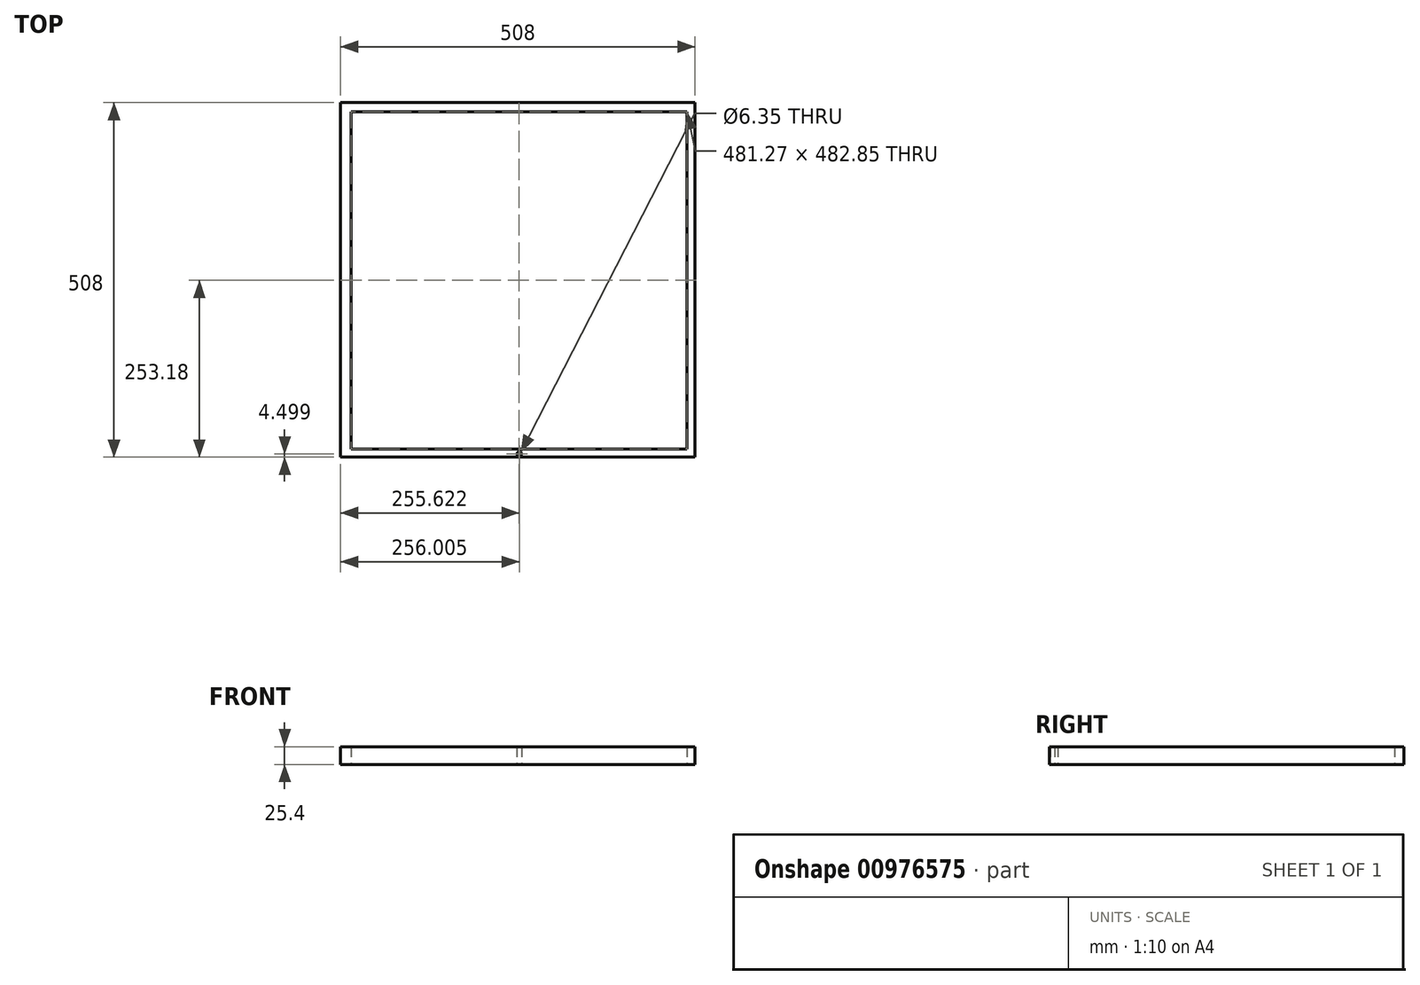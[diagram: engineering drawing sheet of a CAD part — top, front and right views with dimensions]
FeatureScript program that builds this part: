
annotation { "Feature Type Name" : "Feature", "Feature Type Description" : "" }
export const myFeature = defineFeature(function(context is Context, id is Id, definition is map)
    precondition{}
    {
        {
            var Q0;
            Q0=qCreatedBy(makeId("Top.planeOp"),FACE);
            var sketch = newSketch(context, id + "F0", { "sketchPlane" : qUnion([Q0])});
            skLineSegment(sketch, "E0.bottom", {"start": v(-306.53, 141.31) * mm, "end": v(-281.13, 141.31) * mm});
            skLineSegment(sketch, "E0.top", {"start": v(-306.53, -112.69) * mm, "end": v(-281.13, -112.69) * mm});
            skLineSegment(sketch, "E0.left", {"start": v(-306.53, 141.31) * mm, "end": v(-306.53, -112.69) * mm});
            skLineSegment(sketch, "E0.right", {"start": v(-281.13, 141.31) * mm, "end": v(-281.13, -112.69) * mm});
            skSolve(sketch);
        }
        {
            var Q0;
            Q0=makeQuery(id+"F0.imprint","IMPRINT",FACE,{"disambiguationData":[TD([[makeQuery(id+"F0.imprint","IMPRINT",EDGE,{"derivedFrom":sQuery(id+"F0.wireOp",EDGE,"E0.bottom")}),-1.0]])]});
            extrude(context, id + "F1", {"entities" : qUnion([Q0]), "depth" : 5.08 * mm, "offsetDistance" : 25.4 * mm});
        }
        {
            var Q0;
            Q0=makeQuery(id+"F1.opExtrude","SWEPT_BODY",BODY,{"disambiguationData":[OSD([sQuery(id+"F0.wireOp",EDGE,"E0.bottom"),sQuery(id+"F0.wireOp",EDGE,"E0.top"),sQuery(id+"F0.wireOp",EDGE,"E0.left"),sQuery(id+"F0.wireOp",EDGE,"E0.right")])]});
            deleteBodies(context, id + "F2", {"entities" : qUnion([Q0])});
        }
        {
            var Q0;
            Q0=qCreatedBy(makeId("Top.planeOp"),FACE);
            var sketch = newSketch(context, id + "F3", { "sketchPlane" : qUnion([Q0])});
            skLineSegment(sketch, "E1.bottom", {"start": v(-1811.36, 295.79) * mm, "end": v(-1303.36, 295.79) * mm});
            skLineSegment(sketch, "E1.top", {"start": v(-1811.36, -212.21) * mm, "end": v(-1303.36, -212.21) * mm});
            skLineSegment(sketch, "E1.left", {"start": v(-1811.36, 295.79) * mm, "end": v(-1811.36, -212.21) * mm});
            skLineSegment(sketch, "E1.right", {"start": v(-1303.36, 295.79) * mm, "end": v(-1303.36, -212.21) * mm});
            skSolve(sketch);
        }
        {
            var Q0;
            Q0=qCreatedBy(makeId("Top.planeOp"),FACE);
            var sketch = newSketch(context, id + "F4", { "sketchPlane" : qUnion([Q0])});
            skLineSegment(sketch, "E2.bottom", {"start": v(-482.6, 746.05) * mm, "end": v(0, 746.05) * mm});
            skLineSegment(sketch, "E2.top", {"start": v(-482.6, 263.45) * mm, "end": v(0, 263.45) * mm});
            skLineSegment(sketch, "E2.left", {"start": v(-482.6, 746.05) * mm, "end": v(-482.6, 263.45) * mm});
            skLineSegment(sketch, "E2.right", {"start": v(0, 746.05) * mm, "end": v(0, 263.45) * mm});
            skSolve(sketch);
        }
        {
            var Q0;
            Q0=makeQuery(id+"F3.imprint","IMPRINT",FACE,{"disambiguationData":[TD([[makeQuery(id+"F3.imprint","IMPRINT",EDGE,{"derivedFrom":sQuery(id+"F3.wireOp",EDGE,"E1.bottom")}),-1.0]])]});
            var sketch = newSketch(context, id + "F5", { "sketchPlane" : qUnion([Q0])});
            skLineSegment(sketch, "E3.bottom", {"start": v(-1796.37, 282.4) * mm, "end": v(-1315.1, 282.4) * mm});
            skLineSegment(sketch, "E3.top", {"start": v(-1796.37, -200.45) * mm, "end": v(-1315.1, -200.45) * mm});
            skLineSegment(sketch, "E3.left", {"start": v(-1796.37, 282.4) * mm, "end": v(-1796.37, -200.45) * mm});
            skLineSegment(sketch, "E3.right", {"start": v(-1315.1, 282.4) * mm, "end": v(-1315.1, -200.45) * mm});
            skSolve(sketch);
        }
        {
            var Q0;
            Q0=makeQuery(id+"F5.imprint","IMPRINT",FACE,{"disambiguationData":[TD([[makeQuery(id+"F5.imprint","IMPRINT",EDGE,{"derivedFrom":sQuery(id+"F5.wireOp",EDGE,"E3.bottom")}),1.0]])]});
            extrude(context, id + "F6", {"entities" : qUnion([Q0]), "depth" : 25.4 * mm, "offsetDistance" : 25.4 * mm});
        }
        {
            var Q0;
            Q0=makeQuery(id+"F6.opExtrude","CAP_FACE",FACE,{"disambiguationData":[OSD([sQuery(id+"F3.wireOp",EDGE,"E1.bottom"),sQuery(id+"F3.wireOp",EDGE,"E1.top"),sQuery(id+"F3.wireOp",EDGE,"E1.left"),sQuery(id+"F3.wireOp",EDGE,"E1.right"),sQuery(id+"F5.wireOp",EDGE,"E3.bottom"),sQuery(id+"F5.wireOp",EDGE,"E3.top"),sQuery(id+"F5.wireOp",EDGE,"E3.left"),sQuery(id+"F5.wireOp",EDGE,"E3.right")])],"isStart":true});
            var sketch = newSketch(context, id + "F7", { "sketchPlane" : qUnion([Q0])});
            skSolve(sketch);
        }
        {
            var Q0;
            Q0=qCreatedBy(makeId("Top.planeOp"),FACE);
            var sketch = newSketch(context, id + "F8", { "sketchPlane" : qUnion([Q0])});
            skPoint(sketch, "E4", {"position": v(-1555.35, -207.71) * mm});
            skSolve(sketch);
        }
        {
            var Q0;
            Q0=sQuery(id+"F8.wireOp",VERTEX,"E4");
            var Q1;
            Q1=makeQuery(id+"F6.opExtrude","SWEPT_BODY",BODY,{"disambiguationData":[OSD([sQuery(id+"F3.wireOp",EDGE,"E1.bottom"),sQuery(id+"F3.wireOp",EDGE,"E1.top"),sQuery(id+"F3.wireOp",EDGE,"E1.left"),sQuery(id+"F3.wireOp",EDGE,"E1.right"),sQuery(id+"F5.wireOp",EDGE,"E3.bottom"),sQuery(id+"F5.wireOp",EDGE,"E3.top"),sQuery(id+"F5.wireOp",EDGE,"E3.left"),sQuery(id+"F5.wireOp",EDGE,"E3.right")])]});
            hole(context, id + "F9", {"style" : HoleStyle.SIMPLE, "endStyle" : HoleEndStyle.THROUGH, "oppositeDirection" : true, "holeDiameter" : 6.35 * mm, "majorDiameter" : 6.35 * mm, "isTappedThrough" : true, "tappedDepth" : 12.7 * mm, "tapClearance" : 3, "locations" : qUnion([Q0]), "scope" : qUnion([Q1])});
        }
    });
